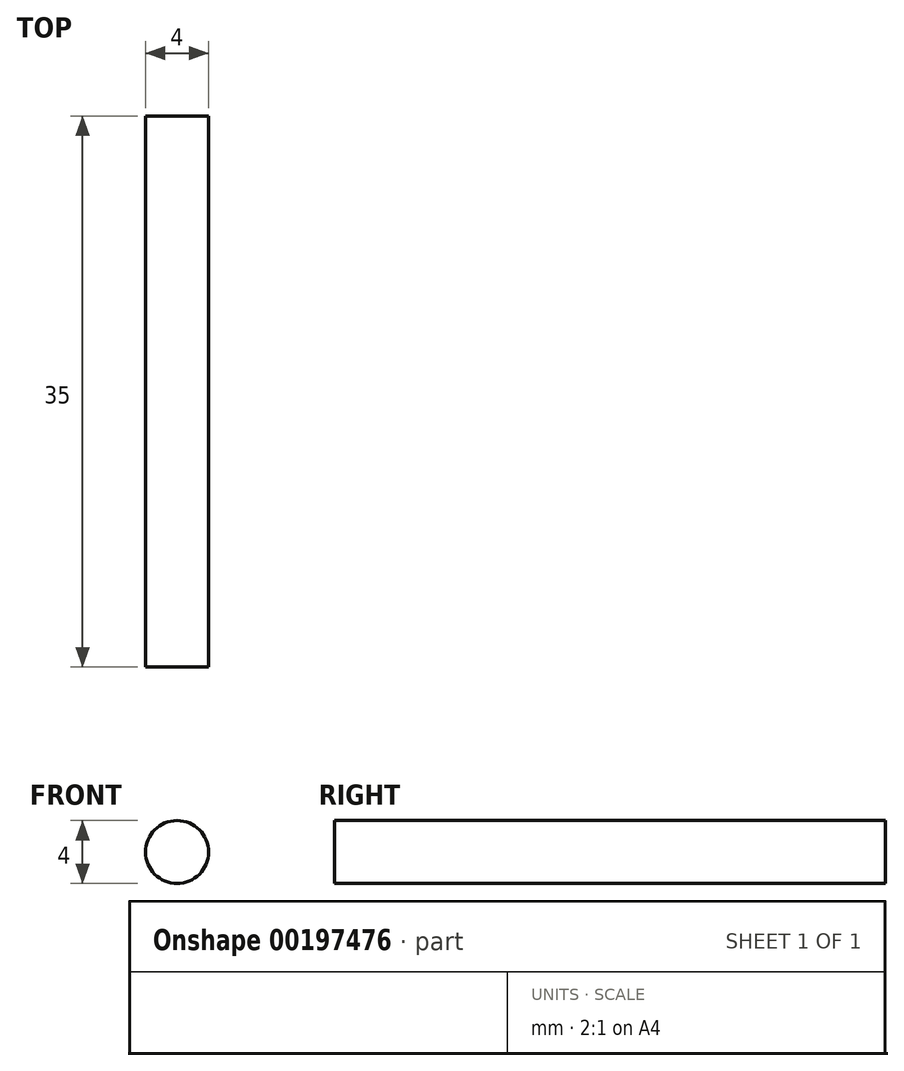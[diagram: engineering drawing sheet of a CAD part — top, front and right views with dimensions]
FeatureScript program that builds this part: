
annotation { "Feature Type Name" : "Feature", "Feature Type Description" : "" }
export const myFeature = defineFeature(function(context is Context, id is Id, definition is map)
    precondition{}
    {
        {
            var Q0;
            Q0=qCreatedBy(makeId("Front.planeOp"),FACE);
            var sketch = newSketch(context, id + "F0", { "sketchPlane" : qUnion([Q0])});
            skCircle(sketch, "E0", {"center": v(0, 0) * mm, "radius": 2 * mm});
            skSolve(sketch);
        }
        {
            var Q0;
            Q0 = qSketchRegion(id + "F0", true);
            extrude(context, id + "F1", {"entities" : qUnion([Q0]), "oppositeDirection" : true, "depth" : 35 * mm});
        }
    });
